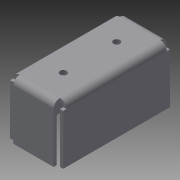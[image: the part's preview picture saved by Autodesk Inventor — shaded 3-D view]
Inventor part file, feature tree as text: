
AUTODESK INVENTOR PART (.ipt)
format: ipt  version: 2013 (Build 170138000, 138)  size: 227,328 bytes
history: native  units: in
note: dims shown in document units (in); Inventor stores cm internally (conversion verified against a paired STEP export)
features: sheet_metal_op x7, sketch x5, other x5, mirror x1, hole x1
ambient origin geometry x8: Origin, YZ Plane, XZ Plane, XY Plane, X Axis, Y Axis, Z Axis, Center Point
bodies: Solid1 (feature_tree)
feature tree (19):
  sheet_metal_op  "Face1"
  sheet_metal_op  "Face2"
  sheet_metal_op  "Face3"
  sheet_metal_op  "Face4"
  mirror  "Mirror5"
  hole  "Hole3"  [1 undecoded]
  sketch  "Sketch1"  dims[d0=0.875in d1=4.0in]
  other  "Plate1"
  sketch  "Sketch10"  dims[d2=0.12in]
  other  "Plate5"
  sheet_metal_op  "Bend4"
  sketch  "Sketch11"  dims[d70=2.0in]
  other  "Plate6"
  sheet_metal_op  "Bend5"
  sketch  "Sketch12"  dims[d72=0.12in]
  other  "Plate7"
  sheet_metal_op  "Bend6"
  sketch  "Sketch13"  dims[d73=0.12in d74=0.06in d75=0.24in d76=0.12in d77=0.12in d78=0.12in d79=0.06in d80=0.24in d81=0.12in d82=0.12in d83=0.12in d84=0.06in d85=0.24in d86=0.12in d88=2.0in d90=0.88in d91=0.88in d92=0.25in d93=0.75in d94=0.375in d95=0.25in d96=0.5635in d97=0.12in d98=0.8108in d99=0.755in d100=0.755in]
  other  "Definition1"
note: 1 required parameter value undecoded (feature->parameter linkage not recoverable at this tier; creation-order binding heuristic only, values carry confidence <= 0.55)
